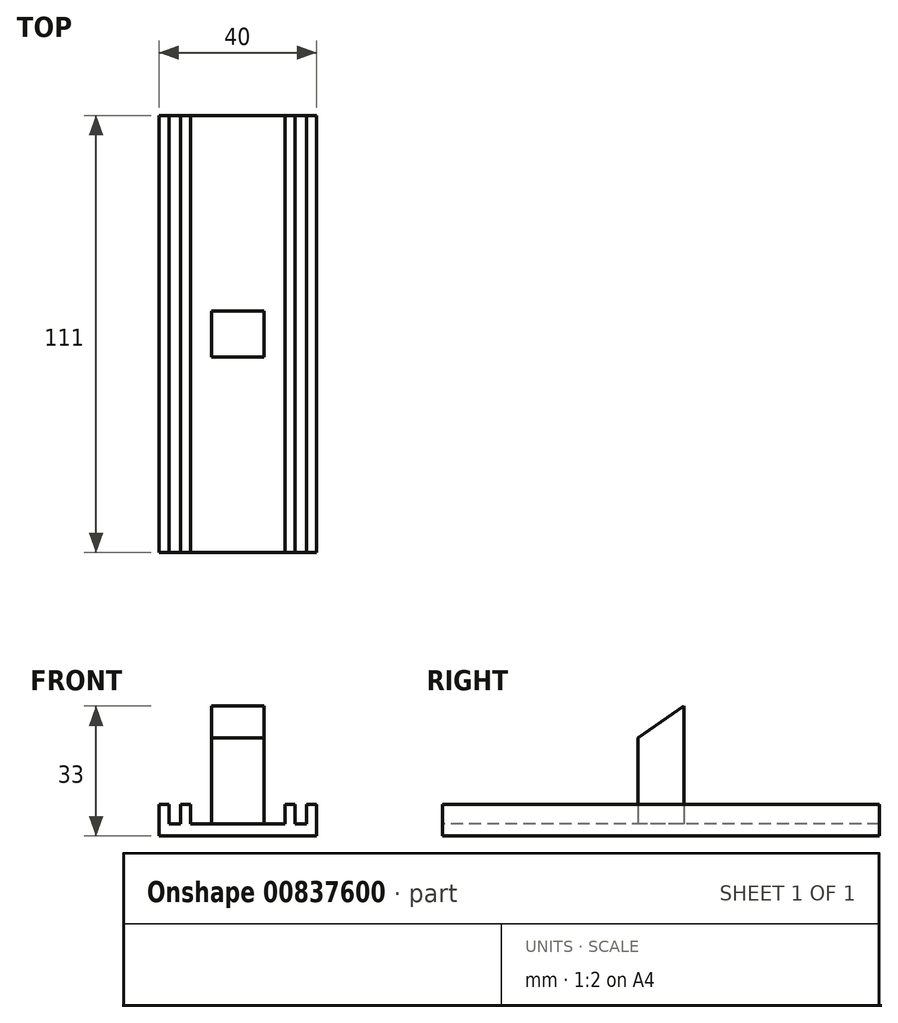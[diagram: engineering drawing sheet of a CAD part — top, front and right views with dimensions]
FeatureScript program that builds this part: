
annotation { "Feature Type Name" : "Feature", "Feature Type Description" : "" }
export const myFeature = defineFeature(function(context is Context, id is Id, definition is map)
    precondition{}
    {
        {
            var Q0;
            Q0=qCreatedBy(makeId("Top.planeOp"),FACE);
            var sketch = newSketch(context, id + "F0", { "sketchPlane" : qUnion([Q0])});
            skLineSegment(sketch, "E0.bottom", {"start": v(-20, 55.5) * mm, "end": v(20, 55.5) * mm});
            skLineSegment(sketch, "E0.top", {"start": v(-20, -55.5) * mm, "end": v(20, -55.5) * mm});
            skLineSegment(sketch, "E0.left", {"start": v(-20, 55.5) * mm, "end": v(-20, -55.5) * mm});
            skLineSegment(sketch, "E0.right", {"start": v(20, 55.5) * mm, "end": v(20, -55.5) * mm});
            skPoint(sketch, "E0.middle", {"position": v(0, 0) * mm});
            skSolve(sketch);
        }
        {
            var Q0;
            Q0=makeQuery(id+"F0.imprint","IMPRINT",FACE,{"disambiguationData":[TD([[makeQuery(id+"F0.imprint","IMPRINT",EDGE,{"derivedFrom":sQuery(id+"F0.wireOp",EDGE,"E0.bottom")}),-1.0]])]});
            extrude(context, id + "F1", {"entities" : qUnion([Q0]), "depth" : 3 * mm, "offsetDistance" : 25.4 * mm});
        }
        {
            var Q0;
            Q0=makeQuery(id+"F1.opExtrude","CAP_FACE",FACE,{"disambiguationData":[OSD([sQuery(id+"F0.wireOp",EDGE,"E0.bottom"),sQuery(id+"F0.wireOp",EDGE,"E0.top"),sQuery(id+"F0.wireOp",EDGE,"E0.left"),sQuery(id+"F0.wireOp",EDGE,"E0.right")])],"isStart":false});
            var sketch = newSketch(context, id + "F2", { "sketchPlane" : qUnion([Q0])});
            skLineSegment(sketch, "E1.bottom", {"start": v(-20, -55.5) * mm, "end": v(-17.5, -55.5) * mm});
            skLineSegment(sketch, "E1.top", {"start": v(-20, 55.5) * mm, "end": v(-17.5, 55.5) * mm});
            skLineSegment(sketch, "E1.left", {"start": v(-20, -55.5) * mm, "end": v(-20, 55.5) * mm});
            skLineSegment(sketch, "E1.right", {"start": v(-17.5, -55.5) * mm, "end": v(-17.5, 55.5) * mm});
            skLineSegment(sketch, "E2.bottom", {"start": v(-14.5, 55.5) * mm, "end": v(-12, 55.5) * mm});
            skLineSegment(sketch, "E2.top", {"start": v(-14.5, -55.5) * mm, "end": v(-12, -55.5) * mm});
            skLineSegment(sketch, "E2.left", {"start": v(-14.5, 55.5) * mm, "end": v(-14.5, -55.5) * mm});
            skLineSegment(sketch, "E2.right", {"start": v(-12, 55.5) * mm, "end": v(-12, -55.5) * mm});
            skSolve(sketch);
        }
        {
            var Q0;
            Q0=makeQuery(id+"F2.imprint","IMPRINT",FACE,{"disambiguationData":[TD([[makeQuery(id+"F2.imprint","IMPRINT",EDGE,{"derivedFrom":sQuery(id+"F2.wireOp",EDGE,"E2.bottom")}),-1.0]])]});
            var Q1;
            Q1=makeQuery(id+"F2.imprint","IMPRINT",FACE,{"disambiguationData":[TD([[makeQuery(id+"F2.imprint","IMPRINT",EDGE,{"derivedFrom":sQuery(id+"F2.wireOp",EDGE,"E1.bottom")}),1.0]])]});
            extrude(context, id + "F3", {"entities" : qUnion([Q0, Q1]), "operationType" : NewBodyOperationType.ADD, "depth" : 5 * mm, "offsetDistance" : 25.4 * mm});
        }
        {
            var Q0;
            Q0=makeQuery(id+"F1.opExtrude","SWEPT_BODY",BODY,{"disambiguationData":[OSD([sQuery(id+"F0.wireOp",EDGE,"E0.bottom"),sQuery(id+"F0.wireOp",EDGE,"E0.top"),sQuery(id+"F0.wireOp",EDGE,"E0.left"),sQuery(id+"F0.wireOp",EDGE,"E0.right")])]});
            var Q1;
            Q1=qCreatedBy(makeId("Right.planeOp"),FACE);
            mirror(context, id + "F4", {"operationType" : NewBodyOperationType.ADD, "entities" : qUnion([Q0]), "mirrorPlane" : qUnion([Q1])});
        }
        {
            var Q0;
            {var subQ1=makeQuery(id+"F3.opExtrude","SWEPT_FACE",FACE,{"disambiguationData":[OSD([sQuery(id+"F2.wireOp",EDGE,"E2.right")])]});var subQ3=sQuery(id+"F0.wireOp",EDGE,"E0.top");var subQ5=sQuery(id+"F0.wireOp",EDGE,"E0.bottom");var subQ9=sQuery(id+"F0.wireOp",EDGE,"E0.right");Q0=makeQuery(id+"F4.boolean.opBoolean","SPLIT",FACE,{"disambiguationData":[TD([subQ1])],"derivedFrom":makeQuery(id+"F3.boolean.opBoolean","SPLIT",FACE,{"disambiguationData":[TD([makeQuery(id+"F1.opExtrude","SWEPT_FACE",FACE,{"disambiguationData":[OSD([subQ9])]})])],"derivedFrom":makeQuery(id+"F1.opExtrude","CAP_FACE",FACE,{"disambiguationData":[OSD([subQ5,subQ3,sQuery(id+"F0.wireOp",EDGE,"E0.left"),subQ9])],"isStart":false})})});}
            var sketch = newSketch(context, id + "F5", { "sketchPlane" : qUnion([Q0])});
            skLineSegment(sketch, "E3.bottom", {"start": v(6.62, 5.8) * mm, "end": v(-6.62, 5.8) * mm});
            skLineSegment(sketch, "E3.top", {"start": v(6.62, -5.8) * mm, "end": v(-6.62, -5.8) * mm});
            skLineSegment(sketch, "E3.left", {"start": v(6.62, 5.8) * mm, "end": v(6.62, -5.8) * mm});
            skLineSegment(sketch, "E3.right", {"start": v(-6.62, 5.8) * mm, "end": v(-6.62, -5.8) * mm});
            skPoint(sketch, "E3.middle", {"position": v(0, 0) * mm});
            skSolve(sketch);
        }
        {
            var Q0;
            Q0 = qSketchRegion(id + "F5", true);
            extrude(context, id + "F6", {"entities" : qUnion([Q0]), "operationType" : NewBodyOperationType.ADD, "depth" : 30 * mm, "offsetDistance" : 25.4 * mm});
        }
        {
            var Q0;
            Q0=makeQuery(id+"F6.opExtrude","SWEPT_FACE",FACE,{"disambiguationData":[OSD([sQuery(id+"F5.wireOp",EDGE,"E3.right")])]});
            var sketch = newSketch(context, id + "F7", { "sketchPlane" : qUnion([Q0])});
            skLineSegment(sketch, "E4", {"start": v(-5.8, 33) * mm, "end": v(5.8, 24.89) * mm});
            skLineSegment(sketch, "E5", {"start": v(5.8, 24.89) * mm, "end": v(-5.8, 33) * mm});
            skLineSegment(sketch, "E6", {"start": v(5.8, 24.89) * mm, "end": v(-5.8, 24.89) * mm});
            skLineSegment(sketch, "E7", {"start": v(-5.8, 33) * mm, "end": v(5.8, 33) * mm});
            skLineSegment(sketch, "E8", {"start": v(5.8, 33) * mm, "end": v(5.8, 24.89) * mm});
            skSolve(sketch);
        }
        {
            var Q0;
            Q0=makeQuery(id+"F7.imprint","IMPRINT",FACE,{"disambiguationData":[TD([[makeQuery(id+"F7.imprint","IMPRINT",EDGE,{"derivedFrom":sQuery(id+"F7.wireOp",EDGE,"E5")}),-1.0]])]});
            var Q1;
            Q1 = qSketchRegion(id + "F7", true);
            extrude(context, id + "F8", {"entities" : qUnion([Q0, Q1]), "operationType" : NewBodyOperationType.REMOVE, "oppositeDirection" : true, "depth" : 25.4 * mm, "offsetDistance" : 25.4 * mm});
        }
    });
